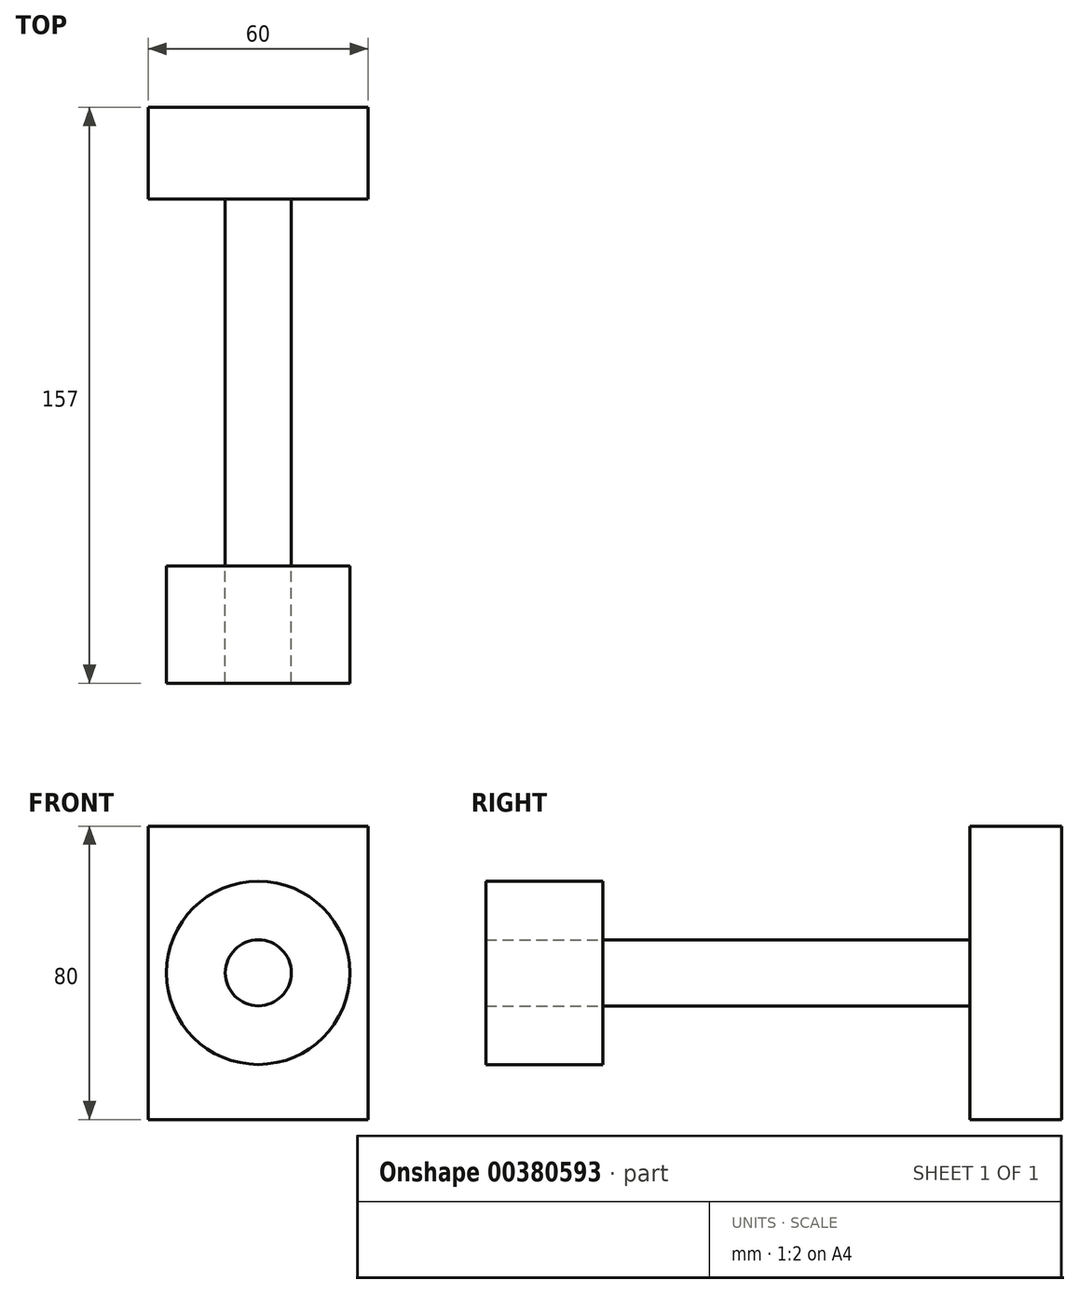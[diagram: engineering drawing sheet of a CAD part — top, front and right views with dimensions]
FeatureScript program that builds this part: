
annotation { "Feature Type Name" : "Feature", "Feature Type Description" : "" }
export const myFeature = defineFeature(function(context is Context, id is Id, definition is map)
    precondition{}
    {
        {
            var Q0;
            Q0=qCreatedBy(makeId("Front.planeOp"),FACE);
            var sketch = newSketch(context, id + "F0", { "sketchPlane" : qUnion([Q0])});
            skCircle(sketch, "E0", {"center": v(0, 0) * mm, "radius": 9 * mm});
            skCircle(sketch, "E1", {"center": v(0, 0) * mm, "radius": 25 * mm});
            skSolve(sketch);
        }
        {
            var Q0;
            Q0 = qSketchRegion(id + "F0", true);
            extrude(context, id + "F1", {"entities" : qUnion([Q0]), "depth" : 32 * mm});
        }
        {
            var Q0;
            Q0=makeQuery(id+"F1.opExtrude","CAP_FACE",FACE,{"disambiguationData":[OSD([sQuery(id+"F0.wireOp",EDGE,"E0"),sQuery(id+"F0.wireOp",EDGE,"E1")])],"isStart":true});
            var sketch = newSketch(context, id + "F2", { "sketchPlane" : qUnion([Q0])});
            skCircle(sketch, "E2", {"center": v(0, 0) * mm, "radius": 9 * mm});
            skSolve(sketch);
        }
        {
            var Q0;
            Q0 = qSketchRegion(id + "F2", true);
            extrude(context, id + "F3", {"entities" : qUnion([Q0]), "depth" : 100 * mm});
        }
        {
            var Q0;
            Q0=makeQuery(id+"F3.opExtrude","CAP_FACE",FACE,{"disambiguationData":[OSD([sQuery(id+"F2.wireOp",EDGE,"E2")])],"isStart":false});
            var sketch = newSketch(context, id + "F4", { "sketchPlane" : qUnion([Q0])});
            skLineSegment(sketch, "E3.bottom", {"start": v(30, -40) * mm, "end": v(-30, -40) * mm});
            skLineSegment(sketch, "E3.top", {"start": v(30, 40) * mm, "end": v(-30, 40) * mm});
            skLineSegment(sketch, "E3.left", {"start": v(30, -40) * mm, "end": v(30, 40) * mm});
            skLineSegment(sketch, "E3.right", {"start": v(-30, -40) * mm, "end": v(-30, 40) * mm});
            skPoint(sketch, "E3.middle", {"position": v(0, 0) * mm});
            skSolve(sketch);
        }
        {
            var Q0;
            Q0 = qSketchRegion(id + "F4", true);
            extrude(context, id + "F5", {"entities" : qUnion([Q0]), "depth" : 25 * mm});
        }
    });
